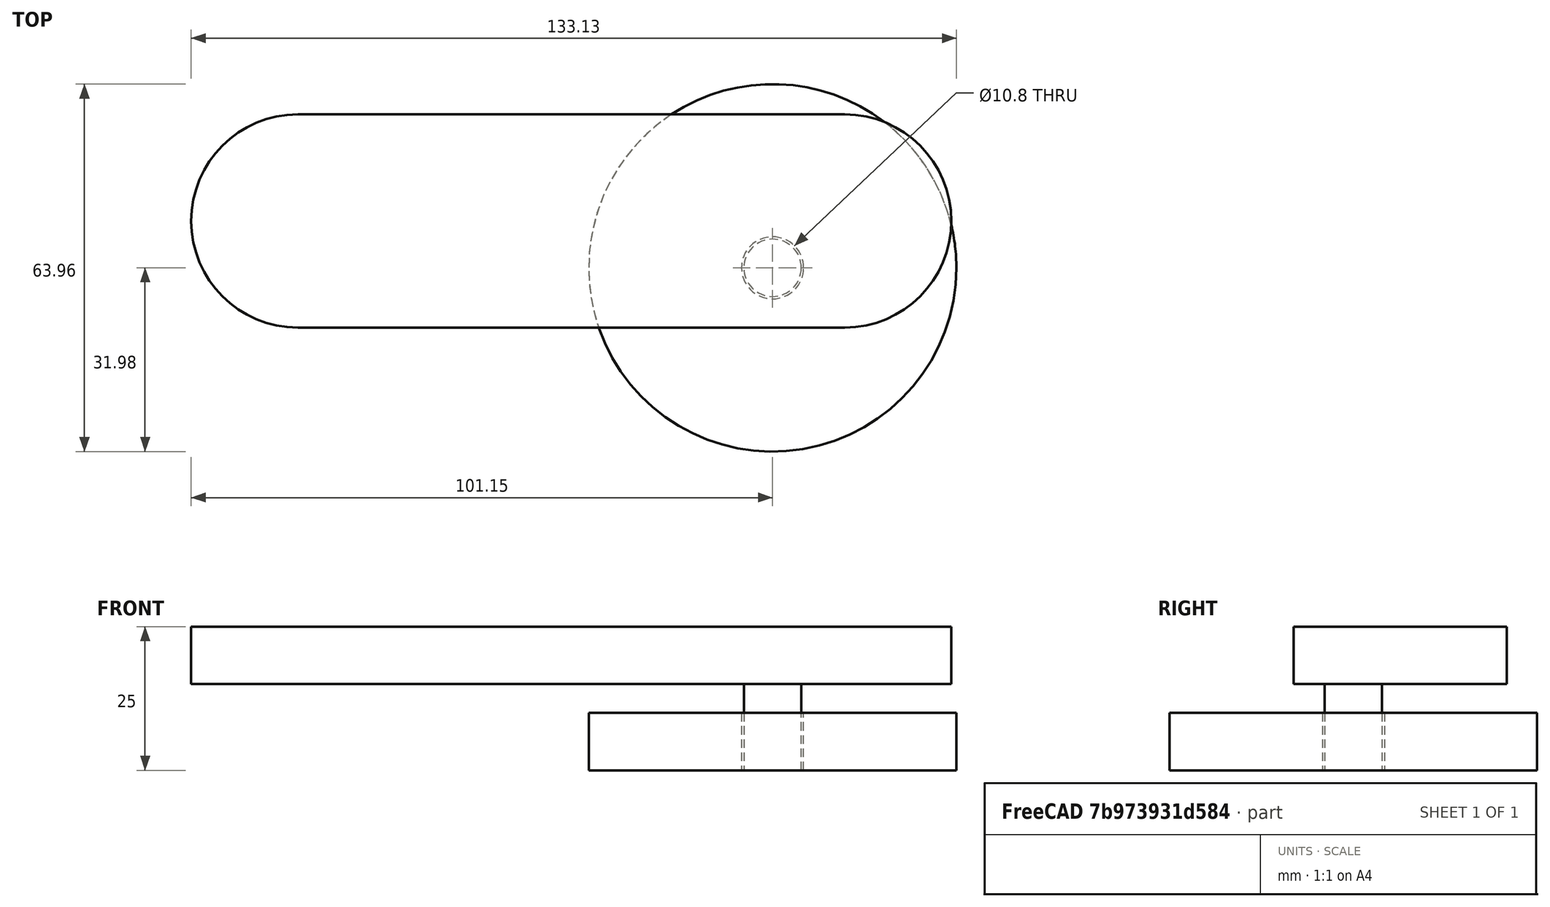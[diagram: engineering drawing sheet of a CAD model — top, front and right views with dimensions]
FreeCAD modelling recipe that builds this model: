
FCSTD DOCUMENT  (FreeCAD 1.0R39109 (Git))
Label: assembly
License: All rights reserved
LicenseURL: https://en.wikipedia.org/wiki/All_rights_reserved
objects: Sketcher::SketchObject×3, PartDesign::Pad×3, PartDesign::Body×3, App::Link×3, App::FeaturePython×3, Assembly::JointGroup×1, Assembly::AssemblyObject×1
note: 18 computed .brp shape members not serialized (recipe doc carries the construction recipe); baked Part::Feature solids carry a one-line shape summary decoded from their .brp

FEATURE [Sketcher::SketchObject] Sketch
  ArcFitTolerance = 1e-06
  AttachmentSupport = -> [XY_Plane]
  FullyConstrained = false
  MakeInternals = false
  MapMode = 5
  sketch-geometry (2):
    g0: Circle CenterX=0 CenterY=0 CenterZ=0 NormalX=0 NormalY=0 NormalZ=1 AngleXU=0 Radius=31.9841
    g1: Circle CenterX=0 CenterY=0 CenterZ=0 NormalX=0 NormalY=0 NormalZ=1 AngleXU=0 Radius=5.40099
  constraints (2):
    c: Coincident(g0,g-1)
    c: Coincident(g1,g0)
FEATURE [PartDesign::Pad] Pad
  Direction = (0,0,1)
  Length = 10
  Length2 = 10
  Profile = -> Sketch
  ReferenceAxis = -> Sketch [N_Axis]
  Refine = true
  Suppressed = false
  Type = 0
FEATURE [PartDesign::Body] Body  label="Cuerpo"
  AllowCompound = false
  Group = -> [Sketch,Pad]
  Origin = -> Origin
  Tip = -> Pad
FEATURE [Sketcher::SketchObject] Sketch001
  ArcFitTolerance = 1e-06
  AttachmentSupport = -> [XY_Plane001]
  FullyConstrained = true
  MakeInternals = false
  MapMode = 5
  sketch-geometry (1):
    g0: Circle CenterX=0 CenterY=0 CenterZ=0 NormalX=0 NormalY=0 NormalZ=1 AngleXU=0 Radius=5
  constraints (2):
    c: Diameter(g0) = 10
    c: Coincident(g0,g-1)
FEATURE [PartDesign::Pad] Pad001
  Direction = (0,0,1)
  Length = 15
  Length2 = 10
  Profile = -> Sketch001
  ReferenceAxis = -> Sketch001 [N_Axis]
  Refine = true
  Suppressed = false
  Type = 0
FEATURE [PartDesign::Body] Body001  label="Cuerpo001"
  AllowCompound = false
  Group = -> [Sketch001,Pad001]
  Origin = -> Origin001
  Tip = -> Pad001
FEATURE [Sketcher::SketchObject] Sketch002
  ArcFitTolerance = 1e-06
  AttachmentSupport = -> [XY_Plane002]
  FullyConstrained = false
  MakeInternals = false
  MapMode = 5
  sketch-geometry (4):
    g0: ArcOfCircle CenterX=12.5522 CenterY=8.15709 CenterZ=0 NormalX=0 NormalY=0 NormalZ=1 AngleXU=0 Radius=18.555 StartAngle=4.71239 EndAngle=7.85398
    g1: ArcOfCircle CenterX=-82.5935 CenterY=8.15709 CenterZ=0 NormalX=0 NormalY=0 NormalZ=1 AngleXU=0 Radius=18.555 StartAngle=1.5708 EndAngle=4.71239
    g2: LineSegment StartX=12.5522 StartY=-10.398 StartZ=0 EndX=-82.5935 EndY=-10.398 EndZ=0
    g3: LineSegment StartX=12.5522 StartY=26.7121 StartZ=0 EndX=-82.5935 EndY=26.7121 EndZ=0
  constraints (6):
    c: Tangent(g0,g2) = 1.5708
    c: Tangent(g0,g3) = -1.5708
    c: Tangent(g1,g2) = 1.5708
    c: Tangent(g1,g3) = -1.5708
    c: Equal(g0,g1)
    c: Horizontal(g2)
FEATURE [PartDesign::Pad] Pad002
  Direction = (0,0,1)
  Length = 10
  Length2 = 10
  Profile = -> Sketch002
  ReferenceAxis = -> Sketch002 [N_Axis]
  Refine = true
  Suppressed = false
  Type = 0
FEATURE [PartDesign::Body] Body002  label="Cuerpo002"
  AllowCompound = false
  Group = -> [Sketch002,Pad002]
  Origin = -> Origin002
  Placement = pos=(0,0,15) rot=(0,0,1;0rad)
  Tip = -> Pad002
FEATURE [App::Link] Cuerpo  label="Cuerpo003"
  LinkedObject = -> Body
FEATURE [App::FeaturePython] GroundedJoint  # Assembly grounded joint (typed FeaturePython)
  ObjectToGround = -> Cuerpo
FEATURE [App::Link] Cuerpo001  label="Cuerpo004"
  LinkPlacement = pos=(0,0,10) rot=(0,0,1;0rad)
  LinkedObject = -> Body001
  Placement = pos=(0,0,10) rot=(0,0,1;0rad)
FEATURE [App::Link] Cuerpo002  label="Cuerpo005"
  LinkPlacement = pos=(-35.6807,-4.45782,25) rot=(0.052251,0.998634,0;3.14159rad)
  LinkedObject = -> Body002
  Placement = pos=(-35.6807,-4.45782,25) rot=(0.052251,0.998634,0;3.14159rad)
FEATURE [App::FeaturePython] Joint  label="Fixed"  # Assembly joint (typed FeaturePython)
  Activated = true
  AngleMax = 0
  AngleMin = 0
  Detach1 = false
  Detach2 = false
  Distance = 0
  Distance2 = 0
  EnableAngleMax = false
  EnableAngleMin = false
  EnableLengthMax = false
  EnableLengthMin = false
  JointType = 0 (Fixed)
  LengthMax = 0
  LengthMin = 0
  Placement1 = pos=(0,0,10) rot=(0,0,1;0rad)
  Reference1 = -> Assembly [Cuerpo.Pad.Edge6,Cuerpo.Pad.Edge6]
  Reference2 = -> Assembly [Cuerpo001.Pad001.Edge2,Cuerpo001.Pad001.Edge2]
FEATURE [App::FeaturePython] Joint001  label="Revolute"  # Assembly joint (typed FeaturePython)
  Activated = true
  AngleMax = 0
  AngleMin = 0
  Detach1 = false
  Detach2 = false
  Distance = 0
  Distance2 = 0
  EnableAngleMax = false
  EnableAngleMin = false
  EnableLengthMax = false
  EnableLengthMin = false
  JointType = 1 (Revolute)
  LengthMax = 0
  LengthMin = 0
  Placement1 = pos=(-35.0206,8.15709,0) rot=(0,0,1;0rad)
  Placement2 = pos=(0,0,15) rot=(0,0,1;0rad)
  Reference1 = -> Assembly [Cuerpo002.Pad002.Face5,Cuerpo002.Pad002.Face5]
  Reference2 = -> Assembly [Cuerpo001.Pad001.Edge3,Cuerpo001.Pad001.Edge3]
FEATURE [Assembly::JointGroup] Joints
  Group = -> [GroundedJoint,Joint,Joint001]
FEATURE [Assembly::AssemblyObject] Assembly
  Group = -> [Joints,Cuerpo,GroundedJoint,Cuerpo001,Cuerpo002,Joint,Joint001]
  Origin = -> Origin003
  Type = Assembly
